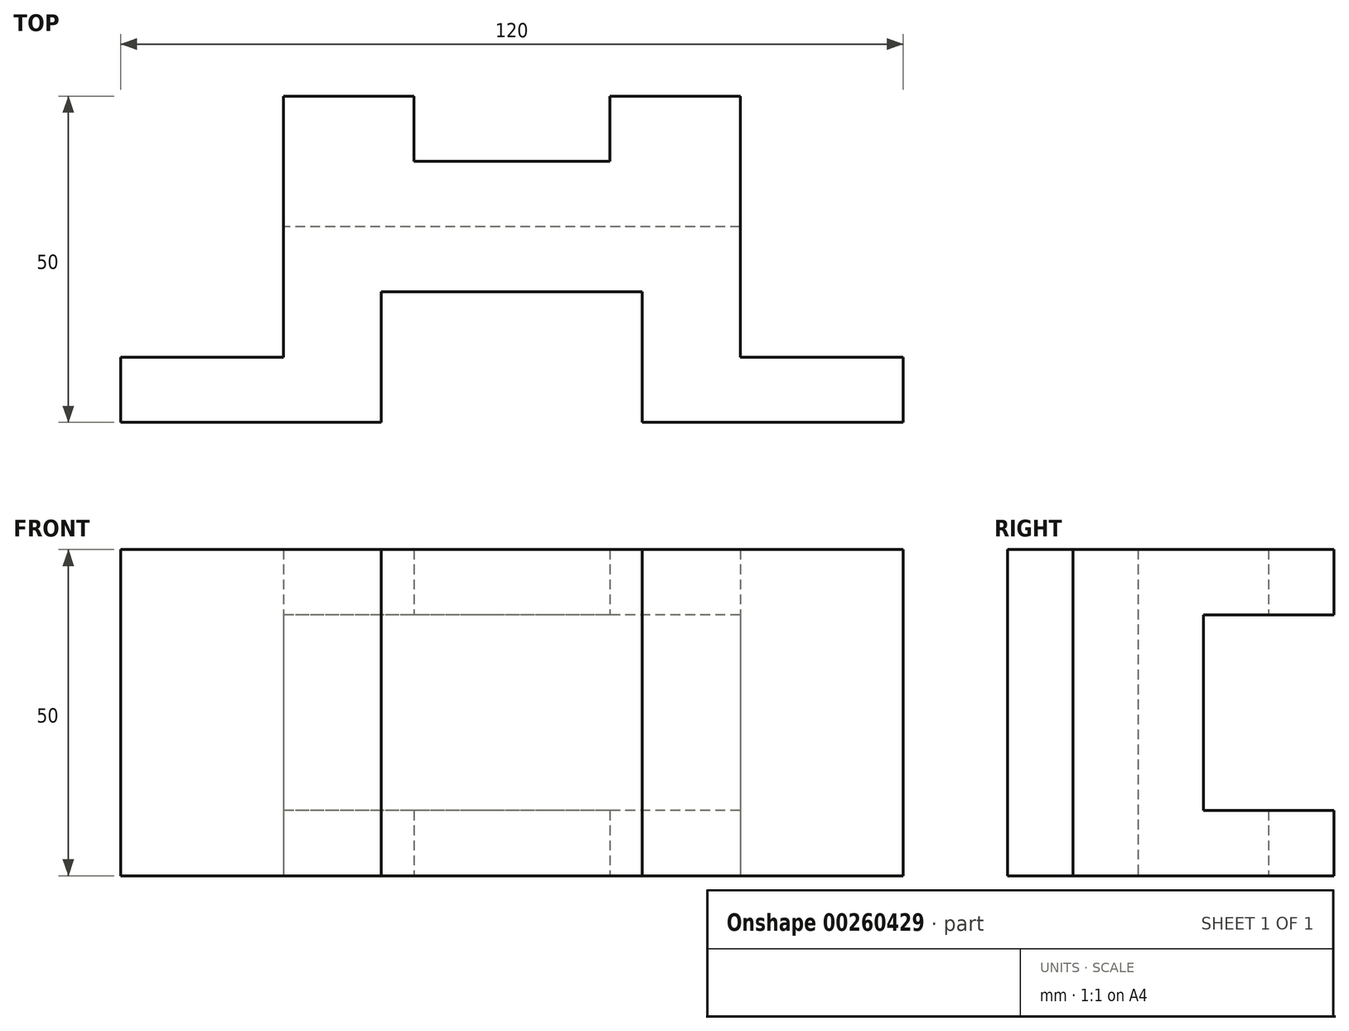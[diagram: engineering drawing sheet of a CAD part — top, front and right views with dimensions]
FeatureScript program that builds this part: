
annotation { "Feature Type Name" : "Feature", "Feature Type Description" : "" }
export const myFeature = defineFeature(function(context is Context, id is Id, definition is map)
    precondition{}
    {
        {
            assignVariable(context, id + "F0", {"name" : "A", "anyValue" : 50});
        }
        {
            var Q0;
            Q0=qCreatedBy(makeId("Top.planeOp"),FACE);
            var sketch = newSketch(context, id + "F1", { "sketchPlane" : qUnion([Q0])});
            skLineSegment(sketch, "E0", {"start": v(-47.54, -30.58) * mm, "end": v(-47.54, -20.58) * mm});
            skLineSegment(sketch, "E1", {"start": v(-47.54, -20.58) * mm, "end": v(-22.54, -20.58) * mm});
            skLineSegment(sketch, "E2", {"start": v(-22.54, -20.58) * mm, "end": v(-22.54, 19.42) * mm});
            skLineSegment(sketch, "E3", {"start": v(-22.54, 19.42) * mm, "end": v(-2.54, 19.42) * mm});
            skLineSegment(sketch, "E4", {"start": v(-2.54, 19.42) * mm, "end": v(-2.54, 9.42) * mm});
            skLineSegment(sketch, "E5", {"start": v(-2.54, 9.42) * mm, "end": v(27.46, 9.42) * mm});
            skLineSegment(sketch, "E6", {"start": v(27.46, 9.42) * mm, "end": v(27.46, 19.42) * mm});
            skLineSegment(sketch, "E7", {"start": v(27.46, 19.42) * mm, "end": v(47.46, 19.42) * mm});
            skLineSegment(sketch, "E8", {"start": v(47.46, 19.42) * mm, "end": v(47.46, -20.58) * mm});
            skLineSegment(sketch, "E9", {"start": v(47.46, -20.58) * mm, "end": v(72.46, -20.58) * mm});
            skLineSegment(sketch, "E10", {"start": v(72.46, -20.58) * mm, "end": v(72.46, -30.58) * mm});
            skLineSegment(sketch, "E11", {"start": v(72.46, -30.58) * mm, "end": v(32.46, -30.58) * mm});
            skLineSegment(sketch, "E12", {"start": v(32.46, -30.58) * mm, "end": v(32.46, -10.58) * mm});
            skLineSegment(sketch, "E13", {"start": v(32.46, -10.58) * mm, "end": v(-7.54, -10.58) * mm});
            skLineSegment(sketch, "E14", {"start": v(-7.54, -10.58) * mm, "end": v(-7.54, -30.58) * mm});
            skLineSegment(sketch, "E15", {"start": v(-7.54, -30.58) * mm, "end": v(-47.54, -30.58) * mm});
            skSolve(sketch);
        }
        {
            var Q0;
            Q0=makeQuery(id+"F1.imprint","IMPRINT",FACE,{"disambiguationData":[TD([[makeQuery(id+"F1.imprint","IMPRINT",EDGE,{"derivedFrom":sQuery(id+"F1.wireOp",EDGE,"E0")}),-1.0]])]});
            extrude(context, id + "F2", {"entities" : qUnion([Q0]), "endBound" : BoundingType.SYMMETRIC, "depth" : (getVariable(context, 'A')) * mm});
        }
        {
            var Q0;
            Q0=makeQuery(id+"F2.opExtrude","SWEPT_FACE",FACE,{"disambiguationData":[OSD([sQuery(id+"F1.wireOp",EDGE,"E7")])]});
            var sketch = newSketch(context, id + "F3", { "sketchPlane" : qUnion([Q0])});
            skLineSegment(sketch, "E16.top", {"start": v(-47.46, 15) * mm, "end": v(22.54, 15) * mm});
            skLineSegment(sketch, "E17.top", {"start": v(-47.46, -15) * mm, "end": v(22.54, -15) * mm});
            skLineSegment(sketch, "E17.left", {"start": v(-47.46, 15) * mm, "end": v(-47.46, -15) * mm});
            skLineSegment(sketch, "E17.right", {"start": v(22.54, 15) * mm, "end": v(22.54, -15) * mm});
            skSolve(sketch);
        }
        {
            var Q0;
            {var subQ0=sQuery(id+"F3.wireOp",EDGE,"E17.right");Q0=makeQuery(id+"F3.imprint","IMPRINT",FACE,{"disambiguationData":[TD([[makeQuery(id+"F3.imprint","IMPRINT",EDGE,{"derivedFrom":subQ0}),-1.0]])]});}
            var Q1;
            {var subQ0=sQuery(id+"F3.wireOp",EDGE,"E17.left");Q1=makeQuery(id+"F3.imprint","IMPRINT",FACE,{"disambiguationData":[TD([[makeQuery(id+"F3.imprint","IMPRINT",EDGE,{"derivedFrom":subQ0}),1.0]])]});}
            extrude(context, id + "F4", {"entities" : qUnion([Q0, Q1]), "operationType" : NewBodyOperationType.REMOVE, "oppositeDirection" : true, "depth" : 20 * mm});
        }
    });
